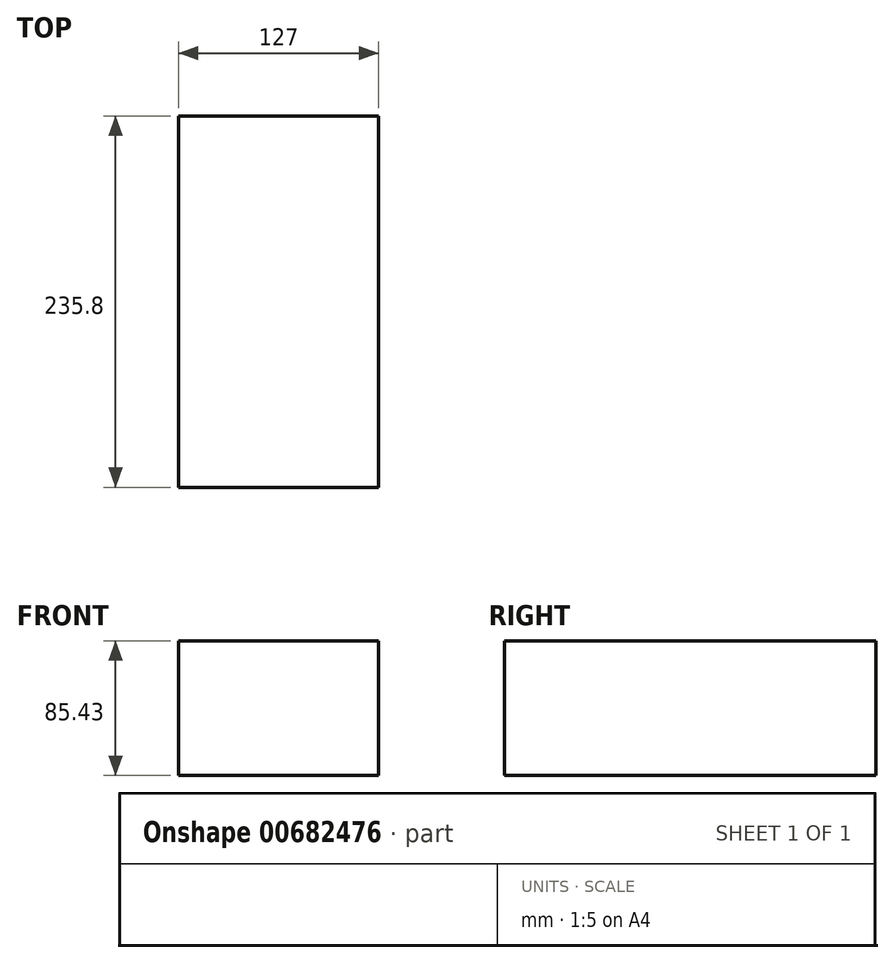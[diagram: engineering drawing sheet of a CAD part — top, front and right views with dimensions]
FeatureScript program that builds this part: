
annotation { "Feature Type Name" : "Feature", "Feature Type Description" : "" }
export const myFeature = defineFeature(function(context is Context, id is Id, definition is map)
    precondition{}
    {
        {
            var Q0;
            Q0=qCreatedBy(makeId("Right.planeOp"),FACE);
            var sketch = newSketch(context, id + "F0", { "sketchPlane" : qUnion([Q0])});
            skLineSegment(sketch, "E0.bottom", {"start": v(0, 0) * mm, "end": v(235.8, 0) * mm});
            skLineSegment(sketch, "E0.top", {"start": v(0, 85.43) * mm, "end": v(235.8, 85.43) * mm});
            skLineSegment(sketch, "E0.left", {"start": v(0, 0) * mm, "end": v(0, 85.43) * mm});
            skLineSegment(sketch, "E0.right", {"start": v(235.8, 0) * mm, "end": v(235.8, 85.43) * mm});
            skSolve(sketch);
        }
        {
            var Q0;
            Q0 = qSketchRegion(id + "F0", true);
            extrude(context, id + "F1", {"entities" : qUnion([Q0]), "depth" : 127 * mm, "offsetDistance" : 25.4 * mm});
        }
    });
